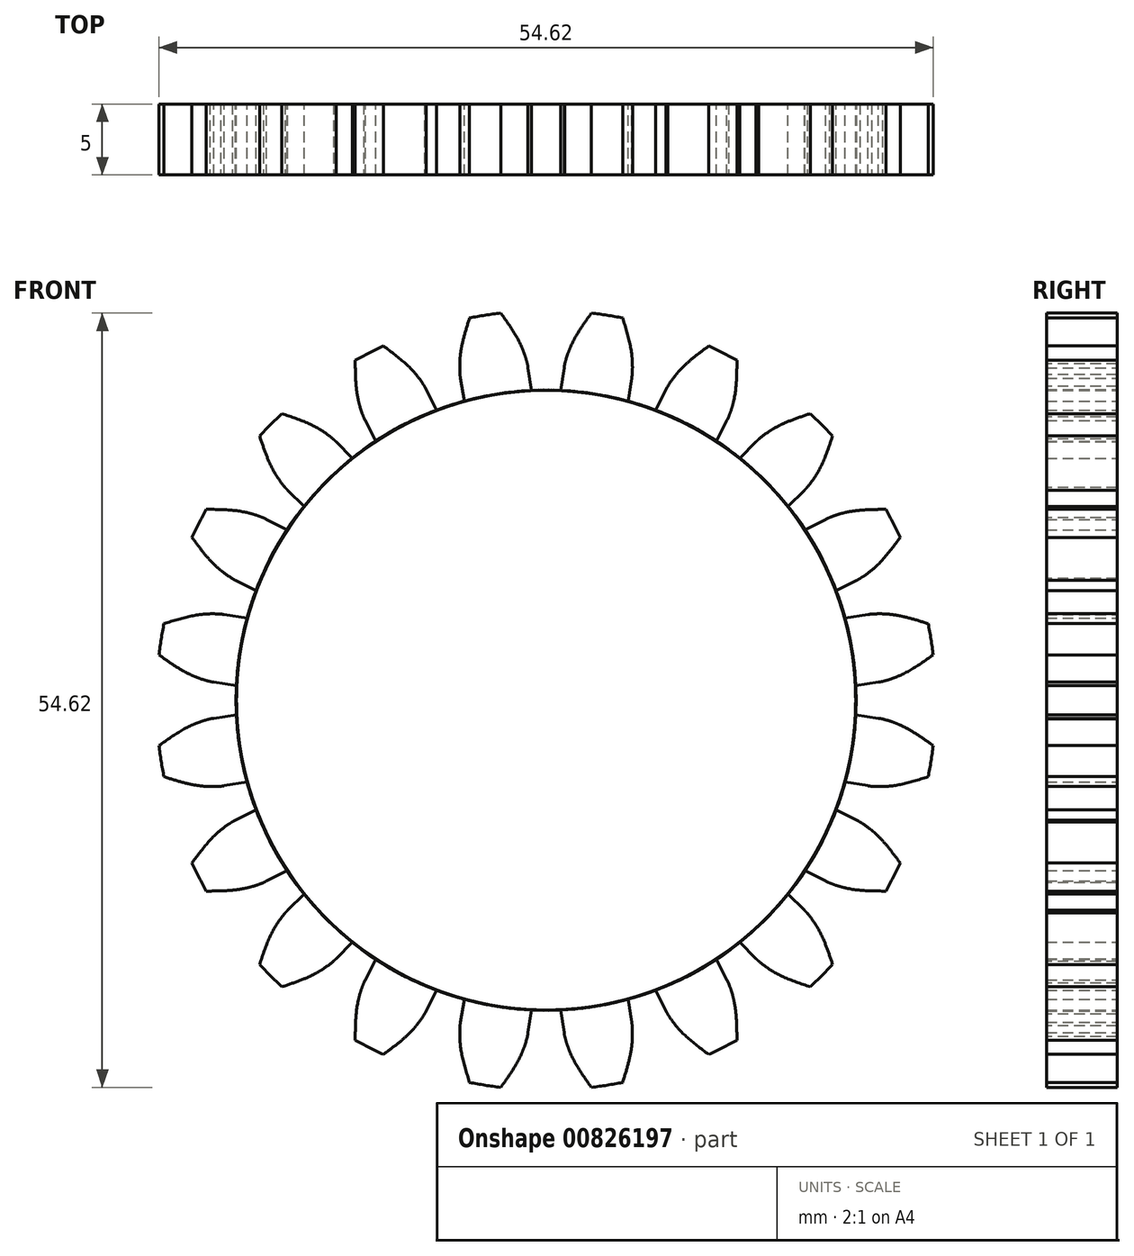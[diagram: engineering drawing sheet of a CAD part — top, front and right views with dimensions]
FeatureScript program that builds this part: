
annotation { "Feature Type Name" : "Feature", "Feature Type Description" : "" }
export const myFeature = defineFeature(function(context is Context, id is Id, definition is map)
    precondition{}
    {
        {
            assignVariable(context, id + "F0", {"name" : "t", "anyValue" : 20});
        }
        {
            var Q0;
            Q0=qCreatedBy(makeId("Front.planeOp"),FACE);
            var sketch = newSketch(context, id + "F1", { "sketchPlane" : qUnion([Q0])});
            skCircle(sketch, "E0", {"center": v(0, 0) * mm, "radius": 25 * mm});
            skCircle(sketch, "E1.0", {"center": v(0, 0) * mm, "radius": 27.5 * mm});
            skCircle(sketch, "E2.0", {"center": v(0, 0) * mm, "radius": 21.88 * mm});
            skLineSegment(sketch, "E3", {"start": v(0, 0) * mm, "end": v(0, 25) * mm, "construction": true});
            skLineSegment(sketch, "E4", {"start": v(-5.4, 26.96) * mm, "end": v(8.03, 22.08) * mm, "construction": true});
            skLineSegment(sketch, "E5", {"start": v(-27.5, 0) * mm, "end": v(27.5, 0) * mm, "construction": true});
            skArc(sketch, "E6", {"start": v(8.03, 22.08) * mm, "mid": v(1.05, 23.47) * mm, "end": v(-6.03, 22.7) * mm});
            skLineSegment(sketch, "E7", {"start": v(-5.4, 26.96) * mm, "end": v(0, 0) * mm});
            skLineSegment(sketch, "E8", {"start": v(0, 0) * mm, "end": v(8.03, 22.08) * mm});
            skLineSegment(sketch, "E9", {"start": v(0, 0) * mm, "end": v(-6.03, 22.7) * mm});
            skLineSegment(sketch, "E10", {"start": v(0, 0) * mm, "end": v(4.6, 23.04) * mm});
            skLineSegment(sketch, "E11", {"start": v(0, 0) * mm, "end": v(1.05, 23.47) * mm});
            skLineSegment(sketch, "E12", {"start": v(0, 0) * mm, "end": v(-2.52, 23.36) * mm});
            skLineSegment(sketch, "E13", {"start": v(4.6, 23.04) * mm, "end": v(-5.92, 25.14) * mm});
            skLineSegment(sketch, "E14", {"start": v(1.05, 23.47) * mm, "end": v(-6.1, 23.79) * mm});
            skLineSegment(sketch, "E15", {"start": v(-2.52, 23.36) * mm, "end": v(-6.07, 22.97) * mm});
            skFitSpline(sketch, "E16", {"points": [v(-5.4, 26.96) * mm, v(-5.92, 25.14) * mm, v(-6.1, 23.79) * mm, v(-6.07, 22.97) * mm, v(-6.03, 22.7) * mm], "startDerivative": vector(-1.71, -5.42) * mm, "endDerivative": vector(0.47, -1.75) * mm});
            skLineSegment(sketch, "E17", {"start": v(0, 0) * mm, "end": v(-5.75, 36.29) * mm, "construction": true});
            skLineSegment(sketch, "E18.MirrorCS", {"start": v(0, 0) * mm, "end": v(-1.28, 23.46) * mm});
            skFitSpline(sketch, "E19.MirrorCS", {"points": [v(-3.2, 27.31) * mm, v(-2.14, 25.73) * mm, v(-1.56, 24.5) * mm, v(-1.32, 23.73) * mm, v(-1.28, 23.46) * mm], "startDerivative": vector(3.3, -4.62) * mm, "endDerivative": vector(0.1, -1.81) * mm});
            skLineSegment(sketch, "E20", {"start": v(-6.03, 22.7) * mm, "end": v(-5.78, 21.1) * mm});
            skLineSegment(sketch, "E21", {"start": v(-1.28, 23.46) * mm, "end": v(-1.02, 21.85) * mm});
            skSolve(sketch);
        }
        {
            var Q0;
            {var subQ0=sQuery(id+"F1.wireOp",EDGE,"E2.0");var subQ1=makeQuery(id+"F1.imprint","INTERSECT",VERTEX,{"derivedFrom":[subQ0,sQuery(id+"F1.wireOp",EDGE,"E20")]});Q0=makeQuery(id+"F1.imprint","IMPRINT",FACE,{"disambiguationData":[TD([[makeQuery(id+"F1.imprint","IMPRINT",EDGE,{"disambiguationData":[TD([[subQ1,1.0]])],"derivedFrom":subQ0}),1.0]])]});}
            var Q1;
            {var subQ0=sQuery(id+"F1.wireOp",EDGE,"E10");var subQ1=sQuery(id+"F1.wireOp",EDGE,"E2.0");var subQ2=makeQuery(id+"F1.imprint","INTERSECT",VERTEX,{"derivedFrom":[subQ1,subQ0]});Q1=makeQuery(id+"F1.imprint","IMPRINT",FACE,{"disambiguationData":[TD([[makeQuery(id+"F1.imprint","IMPRINT",EDGE,{"disambiguationData":[TD([[subQ2,1.0]])],"derivedFrom":subQ1}),1.0]])]});}
            var Q2;
            {var subQ0=sQuery(id+"F1.wireOp",EDGE,"E10");var subQ1=sQuery(id+"F1.wireOp",EDGE,"E2.0");var subQ2=makeQuery(id+"F1.imprint","INTERSECT",VERTEX,{"derivedFrom":[subQ1,subQ0]});Q2=makeQuery(id+"F1.imprint","IMPRINT",FACE,{"disambiguationData":[TD([[makeQuery(id+"F1.imprint","IMPRINT",EDGE,{"disambiguationData":[TD([[subQ2,-1.0]])],"derivedFrom":subQ1}),1.0]])]});}
            var Q3;
            {var subQ0=sQuery(id+"F1.wireOp",EDGE,"E2.0");var subQ1=makeQuery(id+"F1.imprint","INTERSECT",VERTEX,{"derivedFrom":[subQ0,sQuery(id+"F1.wireOp",EDGE,"E21")]});Q3=makeQuery(id+"F1.imprint","IMPRINT",FACE,{"disambiguationData":[TD([[makeQuery(id+"F1.imprint","IMPRINT",EDGE,{"disambiguationData":[TD([[subQ1,1.0]])],"derivedFrom":subQ0}),1.0]])]});}
            var Q4;
            {var subQ0=sQuery(id+"F1.wireOp",EDGE,"E18.MirrorCS");var subQ1=sQuery(id+"F1.wireOp",EDGE,"E2.0");var subQ2=makeQuery(id+"F1.imprint","INTERSECT",VERTEX,{"derivedFrom":[subQ1,subQ0]});Q4=makeQuery(id+"F1.imprint","IMPRINT",FACE,{"disambiguationData":[TD([[makeQuery(id+"F1.imprint","IMPRINT",EDGE,{"disambiguationData":[TD([[subQ2,-1.0]])],"derivedFrom":subQ1}),1.0]])]});}
            var Q5;
            {var subQ0=sQuery(id+"F1.wireOp",EDGE,"E12");var subQ1=sQuery(id+"F1.wireOp",EDGE,"E2.0");var subQ2=makeQuery(id+"F1.imprint","INTERSECT",VERTEX,{"derivedFrom":[subQ1,subQ0]});Q5=makeQuery(id+"F1.imprint","IMPRINT",FACE,{"disambiguationData":[TD([[makeQuery(id+"F1.imprint","IMPRINT",EDGE,{"disambiguationData":[TD([[subQ2,-1.0]])],"derivedFrom":subQ1}),1.0]])]});}
            var Q6;
            {var subQ0=sQuery(id+"F1.wireOp",EDGE,"E7");var subQ1=sQuery(id+"F1.wireOp",EDGE,"E2.0");var subQ2=makeQuery(id+"F1.imprint","INTERSECT",VERTEX,{"derivedFrom":[subQ1,subQ0]});Q6=makeQuery(id+"F1.imprint","IMPRINT",FACE,{"disambiguationData":[TD([[makeQuery(id+"F1.imprint","IMPRINT",EDGE,{"disambiguationData":[TD([[subQ2,-1.0]])],"derivedFrom":subQ1}),1.0]])]});}
            var Q7;
            {var subQ0=sQuery(id+"F1.wireOp",EDGE,"E20");Q7=makeQuery(id+"F1.imprint","IMPRINT",FACE,{"disambiguationData":[TD([[makeQuery(id+"F1.imprint","IMPRINT",EDGE,{"derivedFrom":subQ0}),1.0]])]});}
            var Q8;
            {var subQ0=sQuery(id+"F1.wireOp",EDGE,"E7");var subQ1=sQuery(id+"F1.wireOp",EDGE,"E2.0");var subQ2=makeQuery(id+"F1.imprint","INTERSECT",VERTEX,{"derivedFrom":[subQ1,subQ0]});Q8=makeQuery(id+"F1.imprint","IMPRINT",FACE,{"disambiguationData":[TD([[makeQuery(id+"F1.imprint","IMPRINT",EDGE,{"disambiguationData":[TD([[subQ2,-1.0]])],"derivedFrom":subQ1}),-1.0]])]});}
            var Q9;
            {var subQ1=sQuery(id+"F1.wireOp",EDGE,"E6");var subQ3=sQuery(id+"F1.wireOp",EDGE,"E7");var subQ4=makeQuery(id+"F1.imprint","INTERSECT",VERTEX,{"derivedFrom":[subQ1,subQ3]});Q9=makeQuery(id+"F1.imprint","IMPRINT",FACE,{"disambiguationData":[TD([[makeQuery(id+"F1.imprint","IMPRINT",EDGE,{"disambiguationData":[TD([[subQ4,1.0]])],"derivedFrom":subQ3}),-1.0]])]});}
            var Q10;
            {var subQ0=sQuery(id+"F1.wireOp",EDGE,"E14");var subQ1=sQuery(id+"F1.wireOp",EDGE,"E7");var subQ2=makeQuery(id+"F1.imprint","INTERSECT",VERTEX,{"derivedFrom":[subQ1,subQ0]});Q10=makeQuery(id+"F1.imprint","IMPRINT",FACE,{"disambiguationData":[TD([[makeQuery(id+"F1.imprint","IMPRINT",EDGE,{"disambiguationData":[TD([[subQ2,-1.0]])],"derivedFrom":subQ1}),-1.0]])]});}
            var Q11;
            {var subQ0=sQuery(id+"F1.wireOp",EDGE,"E7");var subQ1=sQuery(id+"F1.wireOp",EDGE,"E0");var subQ2=makeQuery(id+"F1.imprint","INTERSECT",VERTEX,{"derivedFrom":[subQ1,subQ0]});Q11=makeQuery(id+"F1.imprint","IMPRINT",FACE,{"disambiguationData":[TD([[makeQuery(id+"F1.imprint","IMPRINT",EDGE,{"disambiguationData":[TD([[subQ2,-1.0]])],"derivedFrom":subQ1}),1.0]])]});}
            var Q12;
            {var subQ0=sQuery(id+"F1.wireOp",EDGE,"E7");var subQ1=sQuery(id+"F1.wireOp",EDGE,"E0");var subQ2=makeQuery(id+"F1.imprint","INTERSECT",VERTEX,{"derivedFrom":[subQ1,subQ0]});Q12=makeQuery(id+"F1.imprint","IMPRINT",FACE,{"disambiguationData":[TD([[makeQuery(id+"F1.imprint","IMPRINT",EDGE,{"disambiguationData":[TD([[subQ2,-1.0]])],"derivedFrom":subQ1}),-1.0]])]});}
            var Q13;
            {var subQ0=sQuery(id+"F1.wireOp",EDGE,"E16");var subQ3=sQuery(id+"F1.wireOp",EDGE,"E13");var subQ5=makeQuery(id+"F1.imprint","INTERSECT",VERTEX,{"derivedFrom":[subQ3,subQ0]});Q13=makeQuery(id+"F1.imprint","IMPRINT",FACE,{"disambiguationData":[TD([[makeQuery(id+"F1.imprint","IMPRINT",EDGE,{"disambiguationData":[TD([[subQ5,1.0]])],"derivedFrom":subQ3}),-1.0]])]});}
            var Q14;
            {var subQ3=sQuery(id+"F1.wireOp",EDGE,"E13");var subQ7=sQuery(id+"F1.wireOp",EDGE,"E0");var subQ9=makeQuery(id+"F1.imprint","INTERSECT",VERTEX,{"derivedFrom":[subQ7,subQ3]});Q14=makeQuery(id+"F1.imprint","IMPRINT",FACE,{"disambiguationData":[TD([[makeQuery(id+"F1.imprint","IMPRINT",EDGE,{"disambiguationData":[TD([[subQ9,1.0]])],"derivedFrom":subQ7}),-1.0]])]});}
            var Q15;
            {var subQ0=sQuery(id+"F1.wireOp",EDGE,"E13");var subQ1=sQuery(id+"F1.wireOp",EDGE,"E0");var subQ2=makeQuery(id+"F1.imprint","INTERSECT",VERTEX,{"derivedFrom":[subQ1,subQ0]});Q15=makeQuery(id+"F1.imprint","IMPRINT",FACE,{"disambiguationData":[TD([[makeQuery(id+"F1.imprint","IMPRINT",EDGE,{"disambiguationData":[TD([[subQ2,-1.0]])],"derivedFrom":subQ1}),-1.0]])]});}
            var Q16;
            {var subQ0=sQuery(id+"F1.wireOp",EDGE,"E13");var subQ1=sQuery(id+"F1.wireOp",EDGE,"E0");var subQ2=makeQuery(id+"F1.imprint","INTERSECT",VERTEX,{"derivedFrom":[subQ1,subQ0]});Q16=makeQuery(id+"F1.imprint","IMPRINT",FACE,{"disambiguationData":[TD([[makeQuery(id+"F1.imprint","IMPRINT",EDGE,{"disambiguationData":[TD([[subQ2,-1.0]])],"derivedFrom":subQ1}),1.0]])]});}
            var Q17;
            {var subQ0=sQuery(id+"F1.wireOp",EDGE,"E13");var subQ1=sQuery(id+"F1.wireOp",EDGE,"E0");var subQ2=makeQuery(id+"F1.imprint","INTERSECT",VERTEX,{"derivedFrom":[subQ1,subQ0]});Q17=makeQuery(id+"F1.imprint","IMPRINT",FACE,{"disambiguationData":[TD([[makeQuery(id+"F1.imprint","IMPRINT",EDGE,{"disambiguationData":[TD([[subQ2,1.0]])],"derivedFrom":subQ1}),1.0]])]});}
            var Q18;
            {var subQ0=sQuery(id+"F1.wireOp",EDGE,"E21");Q18=makeQuery(id+"F1.imprint","IMPRINT",FACE,{"disambiguationData":[TD([[makeQuery(id+"F1.imprint","IMPRINT",EDGE,{"derivedFrom":subQ0}),-1.0]])]});}
            var Q19;
            {var subQ0=sQuery(id+"F1.wireOp",EDGE,"E18.MirrorCS");var subQ1=sQuery(id+"F1.wireOp",EDGE,"E2.0");var subQ2=makeQuery(id+"F1.imprint","INTERSECT",VERTEX,{"derivedFrom":[subQ1,subQ0]});Q19=makeQuery(id+"F1.imprint","IMPRINT",FACE,{"disambiguationData":[TD([[makeQuery(id+"F1.imprint","IMPRINT",EDGE,{"disambiguationData":[TD([[subQ2,-1.0]])],"derivedFrom":subQ1}),-1.0]])]});}
            var Q20;
            {var subQ3=sQuery(id+"F1.wireOp",EDGE,"E7");var subQ5=sQuery(id+"F1.wireOp",EDGE,"E14");var subQ6=makeQuery(id+"F1.imprint","INTERSECT",VERTEX,{"derivedFrom":[subQ3,subQ5]});Q20=makeQuery(id+"F1.imprint","IMPRINT",FACE,{"disambiguationData":[TD([[makeQuery(id+"F1.imprint","IMPRINT",EDGE,{"disambiguationData":[TD([[subQ6,-1.0]])],"derivedFrom":subQ3}),1.0]])]});}
            var Q21;
            {var subQ1=sQuery(id+"F1.wireOp",EDGE,"E6");var subQ3=sQuery(id+"F1.wireOp",EDGE,"E7");var subQ4=makeQuery(id+"F1.imprint","INTERSECT",VERTEX,{"derivedFrom":[subQ1,subQ3]});Q21=makeQuery(id+"F1.imprint","IMPRINT",FACE,{"disambiguationData":[TD([[makeQuery(id+"F1.imprint","IMPRINT",EDGE,{"disambiguationData":[TD([[subQ4,1.0]])],"derivedFrom":subQ3}),1.0]])]});}
            var Q22;
            {var subQ0=sQuery(id+"F1.wireOp",EDGE,"E12");var subQ1=sQuery(id+"F1.wireOp",EDGE,"E2.0");var subQ2=makeQuery(id+"F1.imprint","INTERSECT",VERTEX,{"derivedFrom":[subQ1,subQ0]});Q22=makeQuery(id+"F1.imprint","IMPRINT",FACE,{"disambiguationData":[TD([[makeQuery(id+"F1.imprint","IMPRINT",EDGE,{"disambiguationData":[TD([[subQ2,-1.0]])],"derivedFrom":subQ1}),-1.0]])]});}
            extrude(context, id + "F2", {"entities" : qUnion([Q0, Q1, Q2, Q3, Q4, Q5, Q6, Q7, Q8, Q9, Q10, Q11, Q12, Q13, Q14, Q15, Q16, Q17, Q18, Q19, Q20, Q21, Q22]), "depth" : 5 * mm, "offsetDistance" : 25 * mm});
        }
        {
            var Q0;
            Q0=qCreatedBy(makeId("Right.planeOp"),FACE);
            var sketch = newSketch(context, id + "F3", { "sketchPlane" : qUnion([Q0])});
            skLineSegment(sketch, "E22", {"start": v(0, 0) * mm, "end": v(-13.34, 0) * mm, "construction": true});
            skSolve(sketch);
        }
        {
            var Q0;
            Q0=makeQuery(id+"F2.opExtrude","SWEPT_BODY",BODY,{"disambiguationData":[OSD([sQuery(id+"F1.wireOp",EDGE,"E1.0"),sQuery(id+"F1.wireOp",EDGE,"E2.0"),sQuery(id+"F1.wireOp",EDGE,"E16"),sQuery(id+"F1.wireOp",EDGE,"E19.MirrorCS"),sQuery(id+"F1.wireOp",EDGE,"E20"),sQuery(id+"F1.wireOp",EDGE,"E21")])]});
            var Q1;
            Q1=sQuery(id+"F3.wireOp",EDGE,"E22");
            circularPattern(context, id + "F4", {"entities" : qUnion([Q0]), "axis" : qUnion([Q1]), "angle" : 360 * degree, "instanceCount" : getVariable(context, 't'), "equalSpace" : true});
        }
    });
